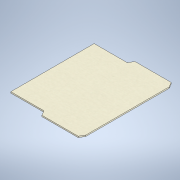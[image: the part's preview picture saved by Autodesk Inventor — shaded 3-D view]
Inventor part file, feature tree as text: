
AUTODESK INVENTOR PART (.ipt)
format: ipt  version: 2021 (Build 250183000, 183)  size: 114,688 bytes
history: native  units: mm
features: extrude x1, sketch x1
ambient origin geometry x8: Origin, YZ Plane, XZ Plane, XY Plane, X Axis, Y Axis, Z Axis, Center Point
bodies: Solid1 (feature_tree)
feature tree (2):
  extrude  "Extrusion1"  Depth=191.0mm
  sketch  "Sketch1"  dims[d3=2.6mm d4=0.0mm d5=191.0mm d6=171.0mm d8=154.0mm d10=120.0deg d11=86.0mm]
